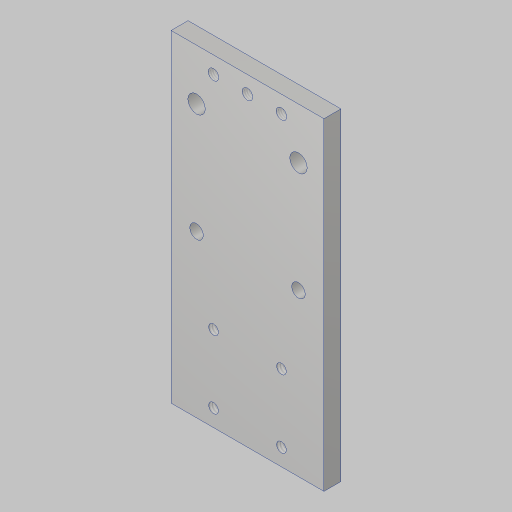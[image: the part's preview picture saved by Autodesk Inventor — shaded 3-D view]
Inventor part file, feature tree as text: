
AUTODESK INVENTOR PART (.ipt)
format: ipt  version: 2023.5 (Build 275446000, 446)  size: 147,968 bytes
history: native  units: in
note: dims shown in document units (in); Inventor stores cm internally (conversion verified against a paired STEP export)
features: hole x3, sketch x2, extrude x1
ambient origin geometry x8: Origin, YZ Plane, XZ Plane, XY Plane, X Axis, Y Axis, Z Axis, Center Point
bodies: Solid1 (feature_tree)
feature tree (6):
  sketch  "Sketch1"  dims[d0=0.257in d1=1.5in]
  extrude  "Extrusion1"  Depth=1.5in
  hole  "Hole1"  [1 undecoded]
  hole  "Hole2"  [1 undecoded]
  hole  "Hole3"  [1 undecoded]
  sketch  "Sketch2"  dims[d4=4.0in d6=0.25in d7=0.0in d8=1.5in d9=2.375in d10=0.201in d11=0.75in d12=0.385in d13=0.25in d14=0.5635in d15=1.0in d16=0.8108in d17=6.0in d18=2.25in d19=0.25in d20=4.75in d21=1.0in d22=0.156in d23=0.38in d24=0.385in d25=0.25in d26=0.5635in d27=1.0in d28=0.8108in d29=0.25in d32=1.0in d33=1.0in d34=0.25in d35=0.145in d36=0.38in d37=0.385in d38=0.25in d39=0.5635in d40=1.0in d41=0.8108in]
note: 3 required parameter values undecoded (feature->parameter linkage not recoverable at this tier; creation-order binding heuristic only, values carry confidence <= 0.55)
